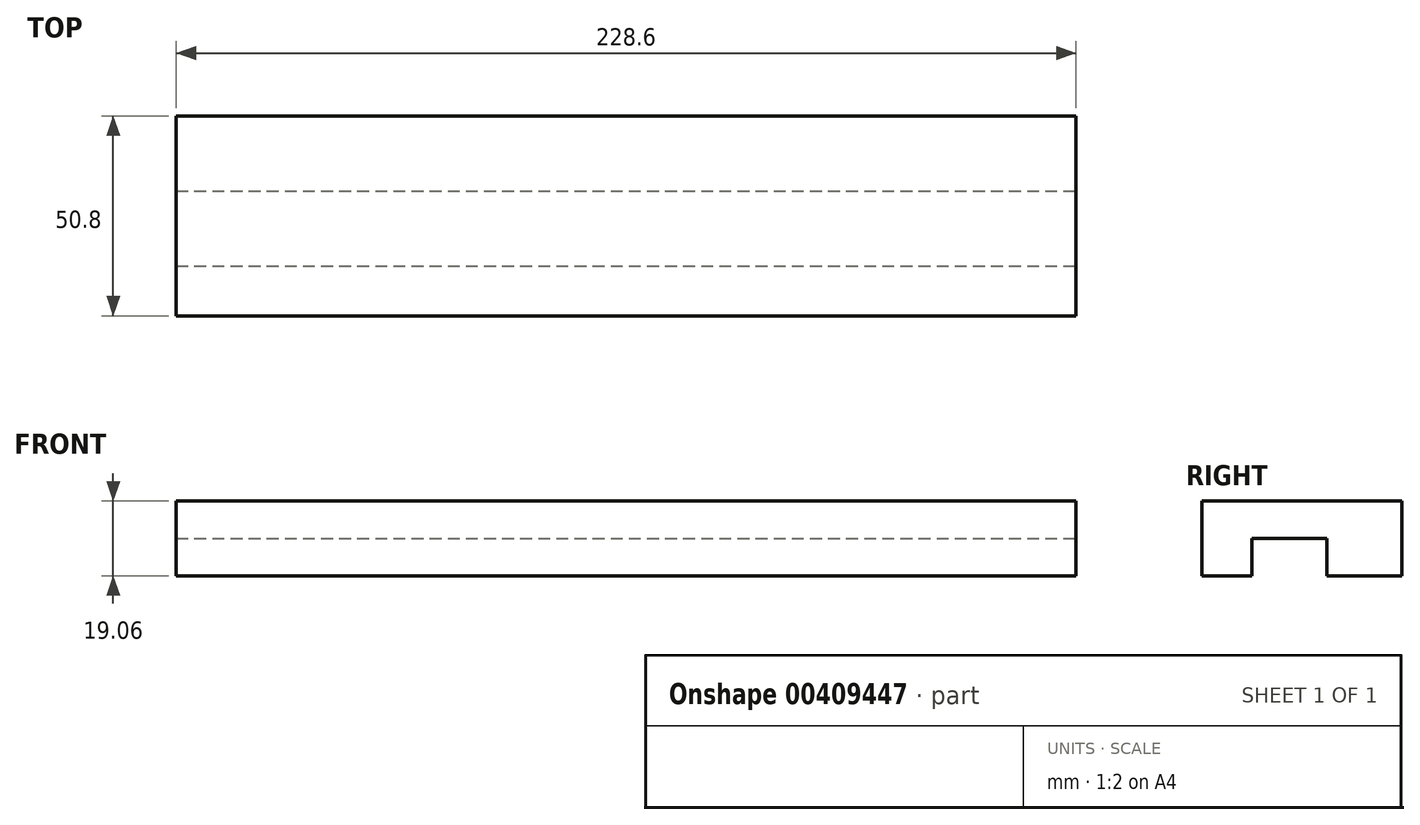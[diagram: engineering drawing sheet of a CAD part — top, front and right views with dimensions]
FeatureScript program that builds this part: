
annotation { "Feature Type Name" : "Feature", "Feature Type Description" : "" }
export const myFeature = defineFeature(function(context is Context, id is Id, definition is map)
    precondition{}
    {
        {
            var Q0;
            Q0=qCreatedBy(makeId("Top.planeOp"),FACE);
            var sketch = newSketch(context, id + "F0", { "sketchPlane" : qUnion([Q0])});
            skLineSegment(sketch, "E0.bottom", {"start": v(-55.56, -23.81) * mm, "end": v(-284.16, -23.81) * mm});
            skLineSegment(sketch, "E0.top", {"start": v(-55.56, 26.99) * mm, "end": v(-284.16, 26.99) * mm});
            skLineSegment(sketch, "E0.left", {"start": v(-55.56, -23.81) * mm, "end": v(-55.56, 26.99) * mm});
            skLineSegment(sketch, "E0.right", {"start": v(-284.16, -23.81) * mm, "end": v(-284.16, 26.99) * mm});
            skLineSegment(sketch, "E1.bottom", {"start": v(-284.16, -11.11) * mm, "end": v(-55.56, -11.11) * mm});
            skLineSegment(sketch, "E1.top", {"start": v(-284.16, 7.94) * mm, "end": v(-55.56, 7.94) * mm});
            skLineSegment(sketch, "E1.left", {"start": v(-284.16, -11.11) * mm, "end": v(-284.16, 7.94) * mm});
            skLineSegment(sketch, "E1.right", {"start": v(-55.56, -11.11) * mm, "end": v(-55.56, 7.94) * mm});
            skLineSegment(sketch, "E2.bottom", {"start": v(-284.16, 26.99) * mm, "end": v(-265.11, 26.99) * mm});
            skLineSegment(sketch, "E2.top", {"start": v(-284.16, -23.81) * mm, "end": v(-265.11, -23.81) * mm});
            skLineSegment(sketch, "E2.left", {"start": v(-284.16, 26.99) * mm, "end": v(-284.16, -23.81) * mm});
            skLineSegment(sketch, "E2.right", {"start": v(-265.11, 26.99) * mm, "end": v(-265.11, -23.81) * mm});
            skLineSegment(sketch, "E3.bottom", {"start": v(-55.56, 26.99) * mm, "end": v(-74.61, 26.99) * mm});
            skLineSegment(sketch, "E3.top", {"start": v(-55.56, -23.81) * mm, "end": v(-74.61, -23.81) * mm});
            skLineSegment(sketch, "E3.left", {"start": v(-55.56, 26.99) * mm, "end": v(-55.56, -23.81) * mm});
            skLineSegment(sketch, "E3.right", {"start": v(-74.61, 26.99) * mm, "end": v(-74.61, -23.81) * mm});
            skSolve(sketch);
        }
        {
            var Q0;
            {var subQ0=sQuery(id+"F0.wireOp",EDGE,"E0.top");Q0=makeQuery(id+"F0.imprint","IMPRINT",FACE,{"disambiguationData":[TD([[makeQuery(id+"F0.imprint","IMPRINT",EDGE,{"derivedFrom":subQ0}),1.0]])]});}
            var Q1;
            {var subQ5=sQuery(id+"F0.wireOp",EDGE,"E2.bottom");Q1=makeQuery(id+"F0.imprint","IMPRINT",FACE,{"disambiguationData":[TD([[makeQuery(id+"F0.imprint","IMPRINT",EDGE,{"derivedFrom":subQ5}),-1.0]])]});}
            var Q2;
            {var subQ0=sQuery(id+"F0.wireOp",EDGE,"E2.right");var subQ1=sQuery(id+"F0.wireOp",EDGE,"E1.bottom");var subQ2=makeQuery(id+"F0.imprint","INTERSECT",VERTEX,{"derivedFrom":[subQ1,subQ0]});Q2=makeQuery(id+"F0.imprint","IMPRINT",FACE,{"disambiguationData":[TD([[makeQuery(id+"F0.imprint","IMPRINT",EDGE,{"disambiguationData":[TD([[subQ2,-1.0]])],"derivedFrom":subQ1}),1.0]])]});}
            var Q3;
            {var subQ0=sQuery(id+"F0.wireOp",EDGE,"E0.bottom");Q3=makeQuery(id+"F0.imprint","IMPRINT",FACE,{"disambiguationData":[TD([[makeQuery(id+"F0.imprint","IMPRINT",EDGE,{"derivedFrom":subQ0}),-1.0]])]});}
            var Q4;
            {var subQ5=sQuery(id+"F0.wireOp",EDGE,"E2.top");Q4=makeQuery(id+"F0.imprint","IMPRINT",FACE,{"disambiguationData":[TD([[makeQuery(id+"F0.imprint","IMPRINT",EDGE,{"derivedFrom":subQ5}),1.0]])]});}
            var Q5;
            {var subQ0=sQuery(id+"F0.wireOp",EDGE,"E2.left");var subQ1=sQuery(id+"F0.wireOp",EDGE,"E1.bottom");var subQ2=makeQuery(id+"F0.imprint","INTERSECT",VERTEX,{"derivedFrom":[subQ1,subQ0]});Q5=makeQuery(id+"F0.imprint","IMPRINT",FACE,{"disambiguationData":[TD([[makeQuery(id+"F0.imprint","IMPRINT",EDGE,{"disambiguationData":[TD([[subQ2,-1.0]])],"derivedFrom":subQ1}),1.0]])]});}
            var Q6;
            {var subQ5=sQuery(id+"F0.wireOp",EDGE,"E3.bottom");Q6=makeQuery(id+"F0.imprint","IMPRINT",FACE,{"disambiguationData":[TD([[makeQuery(id+"F0.imprint","IMPRINT",EDGE,{"derivedFrom":subQ5}),1.0]])]});}
            var Q7;
            {var subQ5=sQuery(id+"F0.wireOp",EDGE,"E3.top");Q7=makeQuery(id+"F0.imprint","IMPRINT",FACE,{"disambiguationData":[TD([[makeQuery(id+"F0.imprint","IMPRINT",EDGE,{"derivedFrom":subQ5}),-1.0]])]});}
            var Q8;
            {var subQ0=sQuery(id+"F0.wireOp",EDGE,"E3.left");var subQ1=sQuery(id+"F0.wireOp",EDGE,"E1.bottom");var subQ2=makeQuery(id+"F0.imprint","INTERSECT",VERTEX,{"derivedFrom":[subQ1,subQ0]});Q8=makeQuery(id+"F0.imprint","IMPRINT",FACE,{"disambiguationData":[TD([[makeQuery(id+"F0.imprint","IMPRINT",EDGE,{"disambiguationData":[TD([[subQ2,1.0]])],"derivedFrom":subQ1}),1.0]])]});}
            extrude(context, id + "F1", {"entities" : qUnion([Q0, Q1, Q2, Q3, Q4, Q5, Q6, Q7, Q8]), "depth" : 9.52 * mm});
        }
        {
            var Q0;
            {var subQ0=sQuery(id+"F0.wireOp",EDGE,"E0.top");Q0=makeQuery(id+"F0.imprint","IMPRINT",FACE,{"disambiguationData":[TD([[makeQuery(id+"F0.imprint","IMPRINT",EDGE,{"derivedFrom":subQ0}),1.0]])]});}
            var Q1;
            {var subQ0=sQuery(id+"F0.wireOp",EDGE,"E0.bottom");Q1=makeQuery(id+"F0.imprint","IMPRINT",FACE,{"disambiguationData":[TD([[makeQuery(id+"F0.imprint","IMPRINT",EDGE,{"derivedFrom":subQ0}),-1.0]])]});}
            extrude(context, id + "F2", {"entities" : qUnion([Q0, Q1]), "operationType" : NewBodyOperationType.ADD, "oppositeDirection" : true, "depth" : 9.52 * mm});
        }
    });
